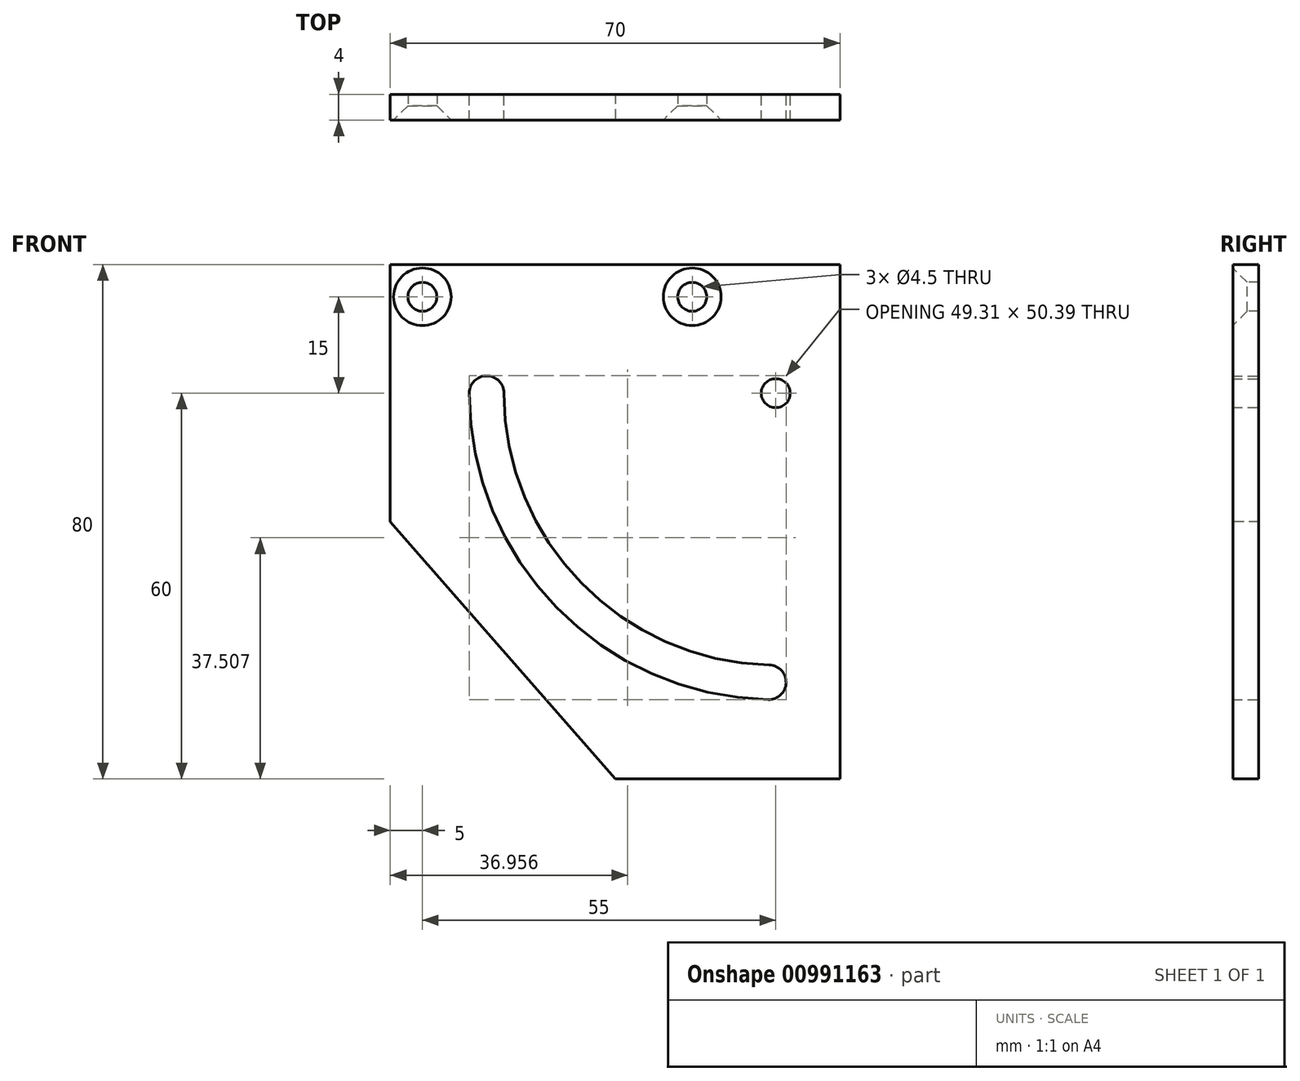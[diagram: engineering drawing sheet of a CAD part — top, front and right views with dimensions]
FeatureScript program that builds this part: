
annotation { "Feature Type Name" : "Feature", "Feature Type Description" : "" }
export const myFeature = defineFeature(function(context is Context, id is Id, definition is map)
    precondition{}
    {
        {
            var Q0;
            Q0=qCreatedBy(makeId("Front.planeOp"),FACE);
            var sketch = newSketch(context, id + "F0", { "sketchPlane" : qUnion([Q0])});
            skLineSegment(sketch, "E0.bottom", {"start": v(0, 0) * mm, "end": v(16.7, 0) * mm});
            skLineSegment(sketch, "E0.top", {"start": v(0, -80) * mm, "end": v(70, -80) * mm});
            skLineSegment(sketch, "E0.left", {"start": v(0, 0) * mm, "end": v(0, -80) * mm});
            skLineSegment(sketch, "E0.right", {"start": v(70, 0) * mm, "end": v(70, -80) * mm});
            skPoint(sketch, "E1", {"position": v(60, -20) * mm});
            skArc(sketch, "E2", {"start": v(15.08, -17.3) * mm, "mid": v(21.58, -43.42) * mm, "end": v(41.82, -61.16) * mm});
            skPoint(sketch, "E3", {"position": v(15, -20) * mm});
            skPoint(sketch, "E4", {"position": v(39.38, -60) * mm});
            skCircle(sketch, "E5", {"center": v(15, -20) * mm, "radius": 2.7 * mm});
            skArc(sketch, "E6", {"start": v(12.3, -20) * mm, "mid": v(19.27, -44.83) * mm, "end": v(38.15, -62.4) * mm});
            skArc(sketch, "E7", {"start": v(17.7, -20) * mm, "mid": v(23.88, -42.02) * mm, "end": v(40.62, -57.6) * mm});
            skLineSegment(sketch, "E8.trimOffspring", {"start": v(19.69, 0) * mm, "end": v(70, 0) * mm});
            skLineSegment(sketch, "E9", {"start": v(0, 0) * mm, "end": v(19.69, 0) * mm});
            skArc(sketch, "E10", {"start": v(15.08, -17.3) * mm, "mid": v(27.8, -51.43) * mm, "end": v(61.61, -64.97) * mm});
            skPoint(sketch, "E11", {"position": v(58.91, -64.99) * mm});
            skArc(sketch, "E12", {"start": v(12.3, -20) * mm, "mid": v(25.87, -53.32) * mm, "end": v(58.85, -67.69) * mm});
            skArc(sketch, "E13", {"start": v(17.7, -20) * mm, "mid": v(29.73, -49.55) * mm, "end": v(58.98, -62.29) * mm});
            skCircle(sketch, "E14", {"center": v(58.91, -64.99) * mm, "radius": 2.7 * mm});
            skSolve(sketch);
        }
        {
            var Q0;
            Q0 = qSketchRegion(id + "F0", true);
            extrude(context, id + "F1", {"entities" : qUnion([Q0]), "depth" : 4 * mm, "offsetDistance" : 25 * mm});
        }
        {
            var Q0;
            Q0=sQuery(id+"F0.wireOp",VERTEX,"E1");
            var Q1;
            Q1=makeQuery(id+"F1.opExtrude","SWEPT_BODY",BODY,{"disambiguationData":[OSD([sQuery(id+"F0.wireOp",EDGE,"E0.top"),sQuery(id+"F0.wireOp",EDGE,"E0.left"),sQuery(id+"F0.wireOp",EDGE,"E0.right"),sQuery(id+"F0.wireOp",EDGE,"E5"),sQuery(id+"F0.wireOp",EDGE,"e0haD2KS-qVb4-y3OR-Vcf3-r0xU2HArvZaj"),sQuery(id+"F0.wireOp",EDGE,"E6"),sQuery(id+"F0.wireOp",EDGE,"E7"),sQuery(id+"F0.wireOp",EDGE,"E8.trimOffspring"),sQuery(id+"F0.wireOp",EDGE,"E9")])]});
            hole(context, id + "F2", {"style" : HoleStyle.SIMPLE, "endStyle" : HoleEndStyle.THROUGH, "oppositeDirection" : true, "standardTappedOrClearance" : lookupTablePath({ "fit" : "Normal", "standard" : "ISO", "size" : "M4", "type" : "Clearance" }), "standardBlindInLast" : lookupTablePath({ "fit" : "Normal", "standard" : "ISO", "engagement" : "75%", "pitch" : "0.7 mm", "size" : "M4", "type" : "Clearance & tapped" }), "holeDiameter" : 4.5 * mm, "majorDiameter" : 8 * mm, "isTappedThrough" : true, "tappedDepth" : 21.25 * mm, "tapClearance" : 3, "startFromSketch" : true, "locations" : qUnion([Q0]), "scope" : qUnion([Q1])});
        }
        {
            var Q0;
            Q0=makeQuery(id+"F1.opExtrude","CAP_FACE",FACE,{"disambiguationData":[OSD([sQuery(id+"F0.wireOp",EDGE,"E0.top"),sQuery(id+"F0.wireOp",EDGE,"E0.left"),sQuery(id+"F0.wireOp",EDGE,"E0.right"),sQuery(id+"F0.wireOp",EDGE,"E5"),sQuery(id+"F0.wireOp",EDGE,"e0haD2KS-qVb4-y3OR-Vcf3-r0xU2HArvZaj"),sQuery(id+"F0.wireOp",EDGE,"E6"),sQuery(id+"F0.wireOp",EDGE,"E7"),sQuery(id+"F0.wireOp",EDGE,"E8.trimOffspring"),sQuery(id+"F0.wireOp",EDGE,"E9")])],"isStart":false});
            var sketch = newSketch(context, id + "F3", { "sketchPlane" : qUnion([Q0])});
            skPoint(sketch, "E15", {"position": v(5, -5) * mm});
            skPoint(sketch, "E16", {"position": v(47, -5) * mm});
            skSolve(sketch);
        }
        {
            var Q0;
            Q0=sQuery(id+"F3.wireOp",VERTEX,"E15");
            var Q1;
            Q1=sQuery(id+"F3.wireOp",VERTEX,"E16");
            var Q2;
            Q2=makeQuery(id+"F1.opExtrude","SWEPT_BODY",BODY,{"disambiguationData":[OSD([sQuery(id+"F0.wireOp",EDGE,"E0.top"),sQuery(id+"F0.wireOp",EDGE,"E0.left"),sQuery(id+"F0.wireOp",EDGE,"E0.right"),sQuery(id+"F0.wireOp",EDGE,"E5"),sQuery(id+"F0.wireOp",EDGE,"e0haD2KS-qVb4-y3OR-Vcf3-r0xU2HArvZaj"),sQuery(id+"F0.wireOp",EDGE,"E6"),sQuery(id+"F0.wireOp",EDGE,"E7"),sQuery(id+"F0.wireOp",EDGE,"E8.trimOffspring"),sQuery(id+"F0.wireOp",EDGE,"E9")])]});
            hole(context, id + "F4", {"style" : HoleStyle.C_SINK, "endStyle" : HoleEndStyle.THROUGH, "standardTappedOrClearance" : lookupTablePath({ "fit" : "Normal", "standard" : "ISO", "size" : "M4", "type" : "Clearance" }), "standardBlindInLast" : lookupTablePath({ "fit" : "Normal", "standard" : "ISO", "engagement" : "75%", "pitch" : "0.7 mm", "size" : "M4", "type" : "Clearance & tapped" }), "holeDiameter" : 4.5 * mm, "cSinkDiameter" : 8.96 * mm, "cSinkAngle" : 90 * degree, "majorDiameter" : 5 * mm, "isTappedThrough" : true, "tappedDepth" : 21.25 * mm, "tapClearance" : 3, "startFromSketch" : true, "locations" : qUnion([Q0, Q1]), "scope" : qUnion([Q2])});
        }
        {
            var Q0;
            Q0=makeQuery(id+"F1.opExtrude","CAP_FACE",FACE,{"disambiguationData":[OSD([sQuery(id+"F0.wireOp",EDGE,"E0.top"),sQuery(id+"F0.wireOp",EDGE,"E0.left"),sQuery(id+"F0.wireOp",EDGE,"E0.right"),sQuery(id+"F0.wireOp",EDGE,"E5"),sQuery(id+"F0.wireOp",EDGE,"E8.trimOffspring"),sQuery(id+"F0.wireOp",EDGE,"E9"),sQuery(id+"F0.wireOp",EDGE,"E12"),sQuery(id+"F0.wireOp",EDGE,"E13"),sQuery(id+"F0.wireOp",EDGE,"E14")])],"isStart":false});
            var sketch = newSketch(context, id + "F5", { "sketchPlane" : qUnion([Q0])});
            skPoint(sketch, "E17", {"position": v(35, -80) * mm});
            skPoint(sketch, "E18", {"position": v(0, -40) * mm});
            skLineSegment(sketch, "E19", {"start": v(0, -40) * mm, "end": v(35, -80) * mm});
            skLineSegment(sketch, "E20", {"start": v(0, -40) * mm, "end": v(0, -80) * mm});
            skLineSegment(sketch, "E21", {"start": v(0, -80) * mm, "end": v(35, -80) * mm});
            skSolve(sketch);
        }
        {
            var Q0;
            Q0 = qSketchRegion(id + "F5", true);
            extrude(context, id + "F6", {"entities" : qUnion([Q0]), "operationType" : NewBodyOperationType.REMOVE, "oppositeDirection" : true, "depth" : 25 * mm, "offsetDistance" : 25 * mm});
        }
    });
